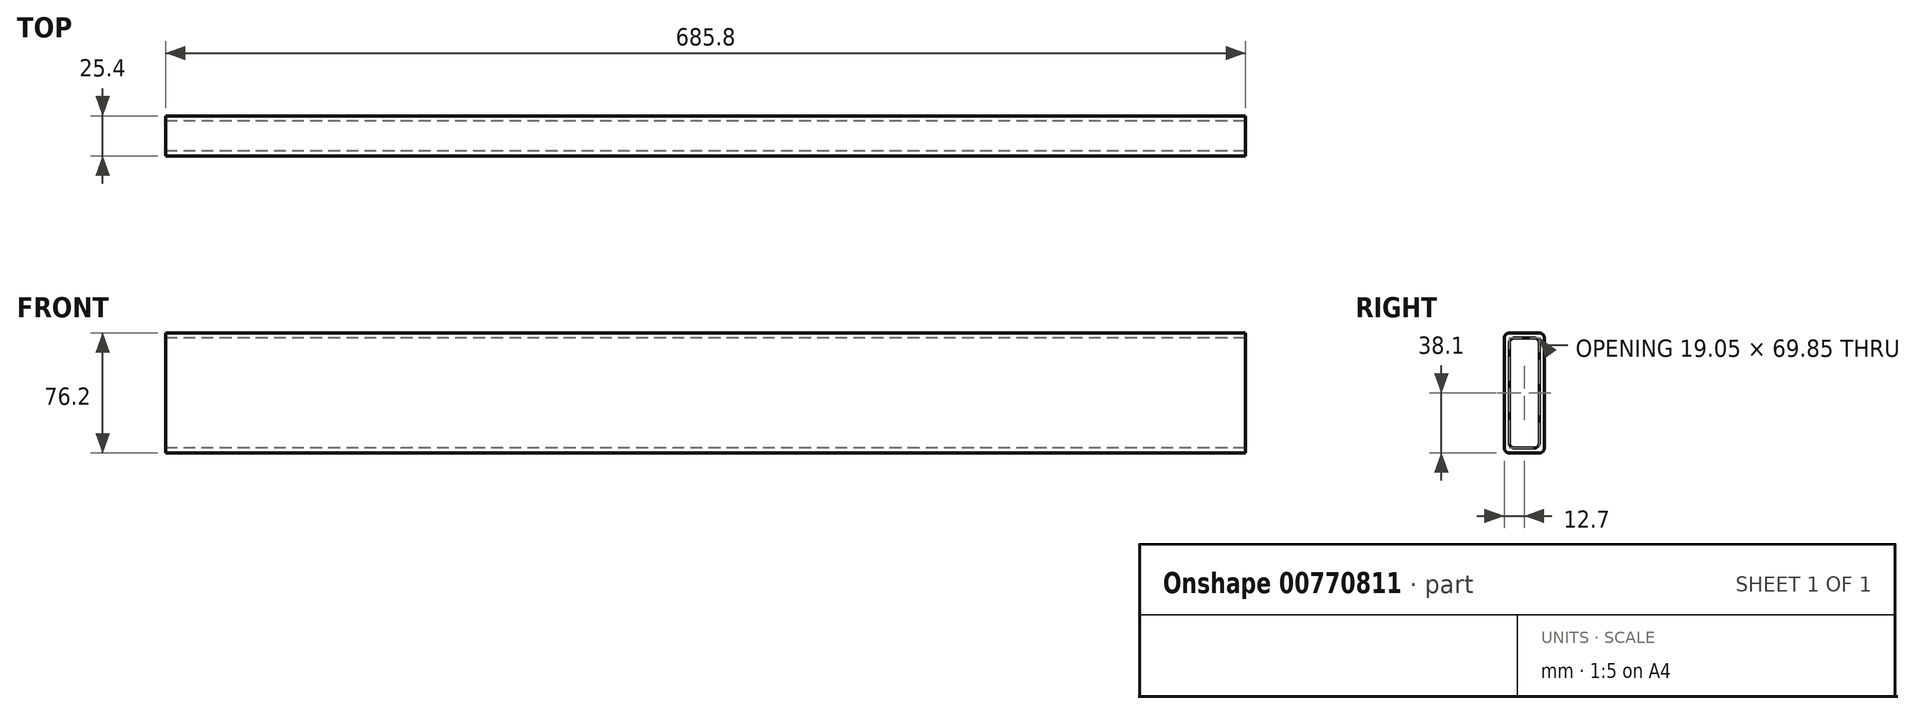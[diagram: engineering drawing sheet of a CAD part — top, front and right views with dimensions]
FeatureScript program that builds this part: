
annotation { "Feature Type Name" : "Feature", "Feature Type Description" : "" }
export const myFeature = defineFeature(function(context is Context, id is Id, definition is map)
    precondition{}
    {
        {
            var Q0;
            Q0=qCreatedBy(makeId("Right.planeOp"),FACE);
            var sketch = newSketch(context, id + "F0", { "sketchPlane" : qUnion([Q0])});
            skLineSegment(sketch, "E0.bottom", {"start": v(3.18, 0) * mm, "end": v(22.23, 0) * mm});
            skLineSegment(sketch, "E0.top", {"start": v(3.18, 76.2) * mm, "end": v(22.22, 76.2) * mm});
            skLineSegment(sketch, "E0.left", {"start": v(0, 3.18) * mm, "end": v(0, 73.03) * mm});
            skLineSegment(sketch, "E0.right", {"start": v(25.4, 3.18) * mm, "end": v(25.4, 73.03) * mm});
            skLineSegment(sketch, "E1.bottom", {"start": v(6.35, 3.18) * mm, "end": v(19.05, 3.18) * mm});
            skLineSegment(sketch, "E1.top", {"start": v(6.35, 73.03) * mm, "end": v(19.05, 73.03) * mm});
            skLineSegment(sketch, "E1.left", {"start": v(3.18, 6.35) * mm, "end": v(3.18, 69.85) * mm});
            skLineSegment(sketch, "E1.right", {"start": v(22.22, 6.35) * mm, "end": v(22.22, 69.85) * mm});
            skPoint(sketch, "E2.visualSharp", {"position": v(25.4, 76.2) * mm});
            skArc(sketch, "E2.filletArc", {"start": v(25.4, 73.03) * mm, "mid": v(24.47, 75.27) * mm, "end": v(22.22, 76.2) * mm});
            skPoint(sketch, "E3.visualSharp", {"position": v(25.4, 0) * mm});
            skArc(sketch, "E3.filletArc", {"start": v(22.23, 0) * mm, "mid": v(24.47, 0.93) * mm, "end": v(25.4, 3.18) * mm});
            skPoint(sketch, "E4.visualSharp", {"position": v(22.23, 3.18) * mm});
            skArc(sketch, "E4.filletArc", {"start": v(19.05, 3.18) * mm, "mid": v(21.3, 4.1) * mm, "end": v(22.22, 6.35) * mm});
            skPoint(sketch, "E5.visualSharp", {"position": v(3.18, 3.18) * mm});
            skArc(sketch, "E5.filletArc", {"start": v(3.18, 6.35) * mm, "mid": v(4.1, 4.1) * mm, "end": v(6.35, 3.18) * mm});
            skPoint(sketch, "E6.visualSharp", {"position": v(0, 0) * mm});
            skArc(sketch, "E6.filletArc", {"start": v(0, 3.18) * mm, "mid": v(0.93, 0.93) * mm, "end": v(3.18, 0) * mm});
            skPoint(sketch, "E7.visualSharp", {"position": v(3.18, 73.03) * mm});
            skArc(sketch, "E7.filletArc", {"start": v(6.35, 73.03) * mm, "mid": v(4.1, 72.1) * mm, "end": v(3.17, 69.85) * mm});
            skPoint(sketch, "E8.visualSharp", {"position": v(0, 76.2) * mm});
            skArc(sketch, "E8.filletArc", {"start": v(3.17, 76.2) * mm, "mid": v(0.93, 75.27) * mm, "end": v(0, 73.03) * mm});
            skArc(sketch, "E9.filletArc", {"start": v(22.22, 69.85) * mm, "mid": v(21.3, 72.1) * mm, "end": v(19.05, 73.03) * mm});
            skSolve(sketch);
        }
        {
            var Q0;
            Q0=makeQuery(id+"F0.imprint","IMPRINT",FACE,{"disambiguationData":[TD([[makeQuery(id+"F0.imprint","IMPRINT",EDGE,{"derivedFrom":sQuery(id+"F0.wireOp",EDGE,"E0.bottom")}),1.0]])]});
            extrude(context, id + "F1", {"entities" : qUnion([Q0]), "depth" : 685.8 * mm, "offsetDistance" : 25.4 * mm});
        }
    });
